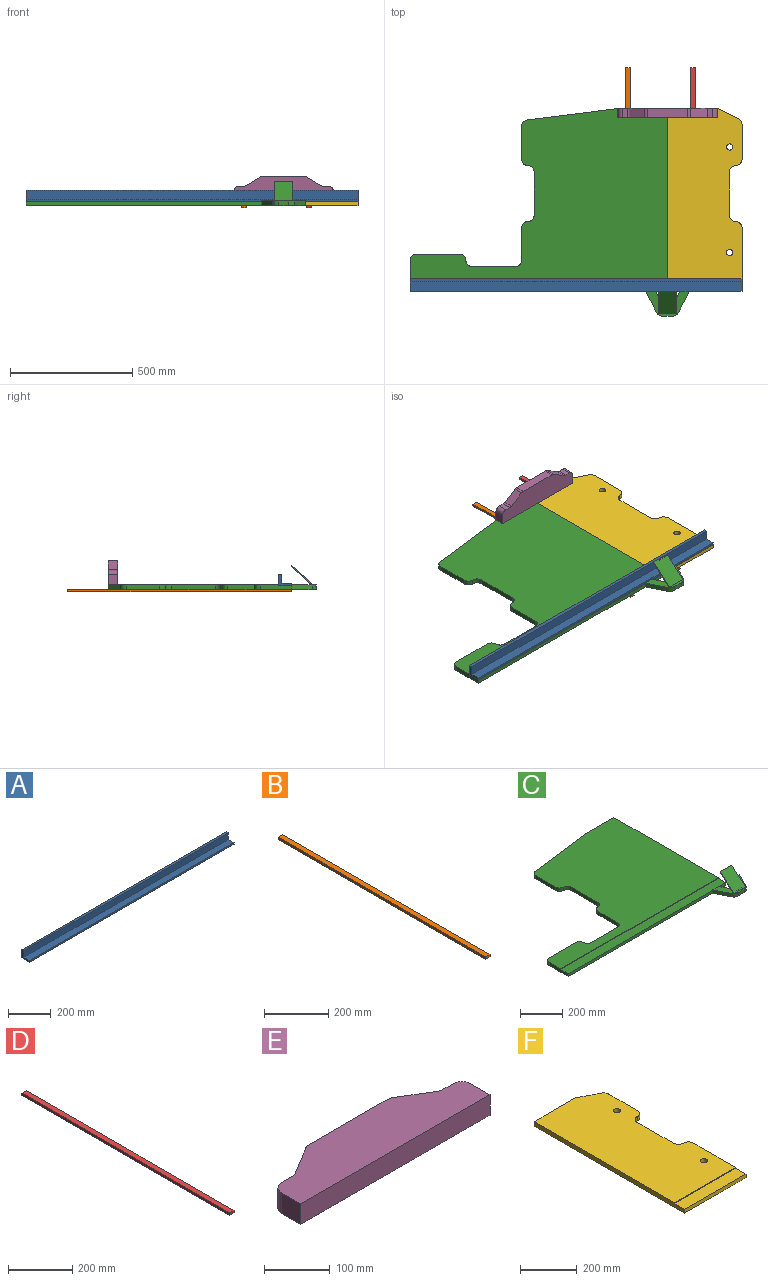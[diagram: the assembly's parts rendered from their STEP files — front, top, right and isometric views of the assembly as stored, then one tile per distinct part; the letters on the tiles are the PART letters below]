
ASSEMBLY  parts=6 mates=5
PART A: 8 faces, bbox 1358.9x50.8x47.6 mm
  f0: plane 1358.9x50.8mm, normal (0,0,-1), area 69032.1mm2, adj f1,f5,f6,f7
  f1: plane 1358.9x47.63mm, normal (0,1,0), area 64717.6mm2, adj f0,f2,f6,f7
  f2: plane 1358.9x12.7mm, normal (0,0,1), area 17258mm2, adj f1,f3,f6,f7
  f3: plane 1358.9x38.1mm, normal (0,-1,0), area 51774.1mm2, adj f2,f4,f6,f7
  f4: plane 1358.9x38.1mm, normal (0,0,1), area 51774.1mm2, adj f3,f5,f6,f7
  f5: plane 1358.9x9.53mm, normal (0,-1,0), area 12943.5mm2, adj f0,f4,f6,f7
  f6: plane 50.8x47.63mm, normal (1,0,0), area 967.7mm2, adj f0,f1,f2,f3,f4,f5
  f7: plane 50.8x47.63mm, normal (-1,0,0), area 967.7mm2, adj f0,f1,f2,f3,f4,f5
PART B: 6 faces, bbox 19.1x914.4x9.5 mm
  f0: plane 914.4x9.53mm, normal (-1,0,0), area 8709.7mm2, adj f1,f3,f4,f5
  f1: plane 19.05x9.53mm, normal (0,-1,0), area 181.5mm2, adj f0,f2,f4,f5
  f2: plane 914.4x9.53mm, normal (1,0,0), area 8709.7mm2, adj f1,f3,f4,f5
  f3: plane 19.05x9.53mm, normal (0,1,0), area 181.5mm2, adj f0,f2,f4,f5
  f4: plane 914.4x19.05mm, normal (0,0,-1), area 17419.3mm2, adj f0,f1,f2,f3
  f5: plane 914.4x19.05mm, normal (0,0,1), area 17419.3mm2, adj f0,f1,f2,f3
PART C: 44 faces, bbox 1143x850.9x99.4 mm
  f0: plane 965.2x15.88mm, normal (0,-1,0), area 15322.6mm2, adj f3,f5,f33,f41
  f1: plane 49.14x15.88mm, normal (0,-1,0), area 780.1mm2, adj f2,f15,f33,f41
  f2: plane 749.3x19.05mm, normal (1,0,0), area 14112.9mm2, adj f1,f4,f16,f33,f41,f43
  f3: plane 127x19.05mm, normal (-1,0,0), area 2258.1mm2, adj f0,f4,f31,f33,f41,f43
  f4: plane 1054.1x698.5mm, normal (0,0,1), area 429734.9mm2, adj f2,f3,f16,f17,f18,f19,f20,f21
  f5: plane 85.45x42.73mm, normal (-0.89,-0.45,0), area 1820mm2, adj f0,f6,f32,f33,f42
  f6: cylinder r=29.21mm len=26.13mm, axis (0,0,-1), area 616.1mm2, adj f5,f7,f32,f33
  f7: plane 40.09x19.05mm, normal (0,-1,0), area 763.8mm2, adj f6,f8,f32,f33
  f8: cylinder r=29.21mm len=26.13mm, axis (0,0,-1), area 616.1mm2, adj f7,f9,f32,f33
  f9: plane 85.45x42.73mm, normal (0.89,-0.45,0), area 1820mm2, adj f8,f10,f32,f33
  f10: plane 39.76x19.05mm, normal (0,1,0), area 757.4mm2, adj f9,f11,f32,f33
  f11: plane 53.4x26.7mm, normal (-0.89,0.45,0), area 1137.4mm2, adj f10,f12,f32,f33
  f12: cylinder r=22.86mm len=20.45mm, axis (0,0,-1), area 482.1mm2, adj f11,f13,f32,f33
  f13: plane 19.05x3.99mm, normal (0,1,0), area 76mm2, adj f12,f14,f32,f33
  f14: cylinder r=22.86mm len=20.45mm, axis (0,0,-1), area 482.1mm2, adj f13,f15,f32,f33
  f15: plane 53.4x26.7mm, normal (0.89,0.45,0), area 1137.4mm2, adj f1,f14,f32,f33,f42
  f16: plane 190.5x19.05mm, normal (0,1,0), area 3629mm2, adj f2,f4,f17,f33
  f17: plane 384.15x48.02mm, normal (-0.12,0.99,0), area 7375mm2, adj f4,f16,f18,f33
  f18: cylinder r=25.4mm len=25.2mm, axis (0,0,-1), area 699.9mm2, adj f4,f17,f19,f33
  f19: plane 136.33x19.05mm, normal (-1,0,0), area 2597mm2, adj f4,f18,f20,f33
  f20: cylinder r=25.4mm len=25.4mm, axis (0,0,-1), area 760.1mm2, adj f4,f19,f21,f33
  f21: cylinder r=25.4mm len=25.4mm, axis (0,0,-1), area 760.1mm2, adj f4,f20,f22,f33
  f22: plane 177.8x19.05mm, normal (-1,0,0), area 3387.1mm2, adj f4,f21,f23,f33
  f23: cylinder r=25.4mm len=25.4mm, axis (0,0,-1), area 760.1mm2, adj f4,f22,f24,f33
  f24: cylinder r=25.4mm len=25.4mm, axis (0,0,-1), area 760.1mm2, adj f4,f23,f25,f33
  f25: plane 133.35x19.05mm, normal (-1,0,0), area 2540.3mm2, adj f4,f24,f26,f33
  f26: cylinder r=25.4mm len=25.4mm, axis (0,0,-1), area 760.1mm2, adj f4,f25,f27,f33
  f27: plane 177.8x19.05mm, normal (0,1,0), area 3387.1mm2, adj f4,f26,f28,f33
  f28: cylinder r=25.4mm len=25.4mm, axis (0,0,-1), area 760.1mm2, adj f4,f27,f29,f33
  f29: cylinder r=25.4mm len=25.4mm, axis (0,0,-1), area 760.1mm2, adj f4,f28,f30,f33
  f30: plane 177.8x19.05mm, normal (0,1,0), area 3387.1mm2, adj f4,f29,f31,f33
  f31: cylinder r=25.4mm len=25.4mm, axis (0,0,-1), area 760.1mm2, adj f3,f4,f30,f33
  f32: plane 177.8x101.6mm, normal (0,0,1), area 8006.8mm2, adj f5,f6,f7,f8,f9,f10,f11,f12
  f33: plane 1143x850.9mm, normal (0,0,-1), area 491833.6mm2, adj f0,f1,f2,f3,f5,f6,f7,f8
  f34: cylinder r=127mm len=76.2mm, axis (-1,0,0), area 1069.5mm2, adj f35,f38,f39,f40
  f35: plane 76.2x21.24mm, normal (0,0.66,-0.75), area 2153.7mm2, adj f34,f36,f39,f40
  f36: plane 76.2x6.26mm, normal (0,1,0), area 477.3mm2, adj f35,f37,f39,f40
  f37: plane 91.56x80.38mm, normal (0,-0.66,0.75), area 9283.8mm2, adj f32,f36,f39,f40
  f38: plane 76.2x52.64mm, normal (0,0.66,-0.75), area 5337.7mm2, adj f32,f34,f39,f40
  f39: plane 91.56x80.38mm, normal (1,0,0), area 549.3mm2, adj f32,f34,f35,f36,f37,f38
  f40: plane 91.56x80.38mm, normal (-1,0,0), area 549.3mm2, adj f32,f34,f35,f36,f37,f38
  f41: plane 1054.1x50.8mm, normal (0,0,1), area 53548.3mm2, adj f0,f1,f2,f3,f42,f43
  f42: plane 39.76x3.18mm, normal (0,1,0), area 126.2mm2, adj f5,f15,f32,f41
  f43: plane 1054.1x3.18mm, normal (0,-1,0), area 3346.8mm2, adj f2,f3,f4,f41
PART D: 6 faces, bbox 19.1x914.4x9.5 mm
  f0: plane 914.4x9.53mm, normal (-1,0,0), area 8709.7mm2, adj f1,f3,f4,f5
  f1: plane 19.05x9.53mm, normal (0,-1,0), area 181.5mm2, adj f0,f2,f4,f5
  f2: plane 914.4x9.53mm, normal (1,0,0), area 8709.7mm2, adj f1,f3,f4,f5
  f3: plane 19.05x9.53mm, normal (0,1,0), area 181.5mm2, adj f0,f2,f4,f5
  f4: plane 914.4x19.05mm, normal (0,0,-1), area 17419.3mm2, adj f0,f1,f2,f3
  f5: plane 914.4x19.05mm, normal (0,0,1), area 17419.3mm2, adj f0,f1,f2,f3
PART E: 16 faces, bbox 406.4x101.6x38.1 mm
  f0: cylinder r=19.05mm len=38.1mm, axis (0,0,-1), area 394.7mm2, adj f1,f13,f14,f15
  f1: plane 38.1x21.68mm, normal (0,1,0), area 825.9mm2, adj f0,f2,f14,f15
  f2: cylinder r=19.05mm len=38.1mm, axis (0,0,-1), area 1140.1mm2, adj f1,f3,f14,f15
  f3: plane 41.28x38.1mm, normal (-1,0,0), area 1572.6mm2, adj f2,f4,f14,f15
  f4: plane 406.4x38.1mm, normal (0,-1,0), area 15483.8mm2, adj f3,f5,f14,f15
  f5: plane 41.28x38.1mm, normal (1,0,0), area 1572.6mm2, adj f4,f6,f14,f15
  f6: cylinder r=19.05mm len=38.1mm, axis (0,0,-1), area 1140.1mm2, adj f5,f7,f14,f15
  f7: plane 38.1x21.68mm, normal (0,1,0), area 825.9mm2, adj f6,f8,f14,f15
  f8: cylinder r=19.05mm len=38.1mm, axis (0,0,-1), area 394.7mm2, adj f7,f9,f14,f15
  f9: plane 59.17x38.1mm, normal (0.52,0.86,0), area 2634.5mm2, adj f8,f10,f14,f15
  f10: cylinder r=19.05mm len=38.1mm, axis (0,0,-1), area 394.7mm2, adj f9,f11,f14,f15
  f11: plane 167.18x38.1mm, normal (0,1,0), area 6369.4mm2, adj f10,f12,f14,f15
  f12: cylinder r=19.05mm len=38.1mm, axis (0,0,-1), area 394.7mm2, adj f11,f13,f14,f15
  f13: plane 59.17x38.1mm, normal (-0.52,0.86,0), area 2634.5mm2, adj f0,f12,f14,f15
  f14: plane 406.4x101.6mm, normal (0,0,1), area 34516.6mm2, adj f0,f1,f2,f3,f4,f5,f6,f7
  f15: plane 406.4x101.6mm, normal (0,0,-1), area 34516.6mm2, adj f0,f1,f2,f3,f4,f5,f6,f7
PART F: 18 faces, bbox 304.8x749.3x19.1 mm
  f0: plane 304.8x15.88mm, normal (0,-1,0), area 4838.7mm2, adj f2,f3,f15,f16
  f1: plane 698.5x304.8mm, normal (0,0,1), area 197654.3mm2, adj f2,f3,f4,f5,f6,f7,f8,f9
  f2: plane 260.35x19.05mm, normal (1,0,0), area 4798.4mm2, adj f0,f1,f4,f15,f16,f17
  f3: plane 749.3x19.05mm, normal (-1,0,0), area 14112.9mm2, adj f0,f1,f12,f15,f16,f17
  f4: cylinder r=25.4mm len=25.4mm, axis (0,0,-1), area 760.1mm2, adj f1,f2,f5,f15
  f5: cylinder r=25.4mm len=25.4mm, axis (0,0,-1), area 760.1mm2, adj f1,f4,f6,f15
  f6: plane 177.8x19.05mm, normal (1,0,0), area 3387.1mm2, adj f1,f5,f7,f15
  f7: cylinder r=25.4mm len=25.4mm, axis (0,0,-1), area 760.1mm2, adj f1,f6,f8,f15
  f8: cylinder r=25.4mm len=25.4mm, axis (0,0,-1), area 760.1mm2, adj f1,f7,f9,f15
  f9: plane 143.05x19.05mm, normal (1,0,0), area 2725.1mm2, adj f1,f8,f10,f15
  f10: cylinder r=25.4mm len=22.72mm, axis (0,0,-1), area 535.7mm2, adj f1,f9,f11,f15
  f11: plane 87.56x43.78mm, normal (0.45,0.89,0), area 1864.9mm2, adj f1,f10,f12,f15
  f12: plane 203.2x19.05mm, normal (0,1,0), area 3871mm2, adj f1,f3,f11,f15
  f13: cylinder r=12.7mm len=25.4mm, axis (0,0,-1), area 1520.1mm2, adj f1,f15
  f14: cylinder r=12.7mm len=25.4mm, axis (0,0,-1), area 1520.1mm2, adj f1,f15
  f15: plane 749.3x304.8mm, normal (0,0,-1), area 213138.1mm2, adj f0,f2,f3,f4,f5,f6,f7,f8
  f16: plane 304.8x50.8mm, normal (0,0,1), area 15483.8mm2, adj f0,f2,f3,f17
  f17: plane 304.8x3.18mm, normal (0,-1,0), area 967.7mm2, adj f1,f2,f3,f16
PLACE A t=(-247.64,265.42,81.79)mm
PLACE B t=(-247.64,265.42,84.97)mm
PLACE C t=(-247.64,265.42,84.97)mm
PLACE D t=(-247.64,265.42,84.97)mm
PLACE E rot(axis=(1,0,0),90deg) t=(-247.64,1014.72,459.62)mm
PLACE F t=(-247.64,265.42,84.97)mm
MATE fastened F.f3 <-> C.f2  axis (-1,0,0) through (-247.64,1014.72,104.02)mm
MATE fastened F.f0 <-> D.f1  axis (0,-1,0) through (-152.39,265.42,84.97)mm
MATE fastened C.f4 <-> E.f4  axis (0,0,1) through (-247.64,1014.72,104.02)mm
MATE fastened B.f1 <-> C.f0  axis (0,-1,0) through (-400.04,265.42,84.97)mm
MATE fastened A.f0 <-> C.f41  axis (0,0,-1) through (-1301.74,316.22,100.84)mm
